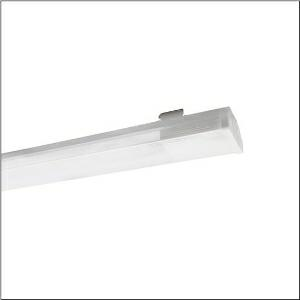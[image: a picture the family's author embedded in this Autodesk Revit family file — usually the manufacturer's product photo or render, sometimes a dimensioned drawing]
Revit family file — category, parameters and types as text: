
# Revit family: modario_r__31_gen_2_53bm8117u4l3d2_7977
name_source: partatom
category: Lighting Fixtures
units: mm (PartAtom-declared; Revit-internal decimal feet)

## family parameters
Cut with Voids When Loaded = No
Host = Face
Light Source = No
Part Type = Normal
Room Calculation Point = No
Round Connector Dimension = Use Diameter
Shared = No

## types (1)
- Modario® 31 Gen.2 (1 x LED, 23600 lm, 126 W, 4000K)
    Apparent Load = 126 VA
    CIE Flux Codes = 50 78 94 90 100
    Color Rendering = 80
    Color Temperature = 4000K
    Default Elevation = 1800 mm
    Description = Modario® 31 Gen.2, luminaire insert, of sheet steel, coil coated, white, length: 2.392mm, width: 81mm, height: 82mm, 8x system unit, system units: 299mm, LED rated luminous flux: 23.600lm, light colour: 840, control gear: ON/OFF, with plug, 3-pole, with phase selection, mains connection: 220..240V, AC, 50/60Hz, rated input power: 126W, through-wiring accessed according to module size, primary optical cover: cover, of PMMA, light emission: direct distribution, primary light characteristic: symmetric, protection rating (complete): IP20, protection rating (LED compartment): IP50, insulation class (complete): insulation class I (protective earthing), certification: CE, ENEC, VDE, UKCA, impact resistance: IK03, permissible ambient temperature for indoor applications: -40..+35°C, corresponds to IFS (International Featured Standards) requirements for safety and quality in the food industry, reducing of maximum allowable ambient temperature of 5°C with ceiling mounting, packaging unit: 1 piece
    Height = 92 mm
    Lamp = 1 x LED
    Lamp Light Flux = 23600 lm
    Lamp Power = 126 W
    Lamp count = 1
    Length = 2392 mm
    Luminous efficacy = 187 lm/W
    Manufacturer = Siteco
    ModVariant = No
    Model = 53BM8117U4L3D2
    Mounting Place = Ceiling
    Mounting Type = Pendant
    Number of Poles = 1
    OnlyDefault = Yes
    Power Factor = 1
    Product Name = Modario® 31 Gen.2
    Product group = luminaire insert
    ProductGroupID = 902
    Protection Class = Protection class I
    Protection Degree = IP 20
    RLX_Detail_Level = 1
    RLX_Emergency_Light_Flux = 0 lm
    RLX_Emergency_Type = 0
    RLX_Emergency_Type_DB = No
    RlxData = <blob elided: 34581 chars, md5=55b59cb3>
    Socket = socket
    Standby Power = 0 W
    System Light Flux = 23600 lm
    System Power = 126 W
    Type Comments = Product without accessories
    Type Image = l_1341883.jpg
    URL = http://relux.com
    VarID = ---
    Voltage = 0 V
    Weight = 0.00 kg
    Width = 81 mm

## geometry (parser evidence)
native form markers: Blend x4, Sweep x14
no freeform markers — native parametric forms only
